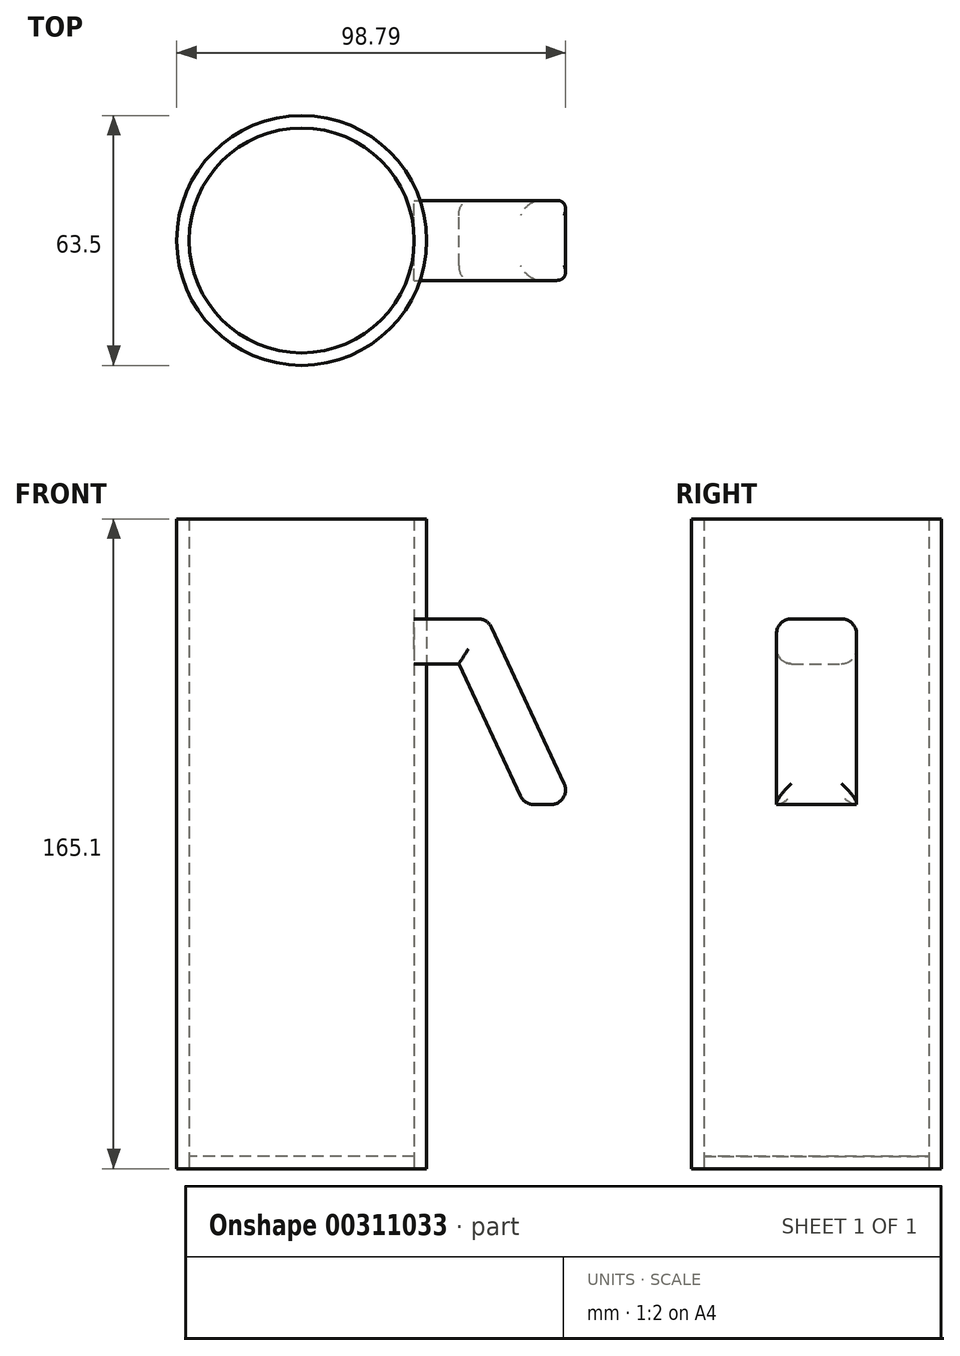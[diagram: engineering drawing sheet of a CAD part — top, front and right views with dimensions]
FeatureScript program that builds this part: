
annotation { "Feature Type Name" : "Feature", "Feature Type Description" : "" }
export const myFeature = defineFeature(function(context is Context, id is Id, definition is map)
    precondition{}
    {
        {
            var Q0;
            Q0=qCreatedBy(makeId("Top.planeOp"),FACE);
            var sketch = newSketch(context, id + "F0", { "sketchPlane" : qUnion([Q0])});
            skCircle(sketch, "E0", {"center": v(0, 0) * mm, "radius": 28.58 * mm});
            skCircle(sketch, "E1", {"center": v(0, 0) * mm, "radius": 31.75 * mm});
            skPoint(sketch, "E2.middle", {"position": v(31.75, 0) * mm});
            skSolve(sketch);
        }
        {
            var Q0;
            Q0=qCreatedBy(makeId("Front.planeOp"),FACE);
            var sketch = newSketch(context, id + "F1", { "sketchPlane" : qUnion([Q0])});
            skLineSegment(sketch, "E3.bottom", {"start": v(28.57, 128.27) * mm, "end": v(39.92, 128.27) * mm});
            skLineSegment(sketch, "E3.top", {"start": v(28.57, 139.7) * mm, "end": v(47.2, 139.7) * mm});
            skLineSegment(sketch, "E3.left", {"start": v(28.57, 128.27) * mm, "end": v(28.57, 139.7) * mm});
            skLineSegment(sketch, "E4", {"start": v(47.2, 139.7) * mm, "end": v(69.22, 92.49) * mm});
            skLineSegment(sketch, "E5", {"start": v(39.92, 128.27) * mm, "end": v(56.6, 92.49) * mm});
            skLineSegment(sketch, "E6", {"start": v(56.6, 92.49) * mm, "end": v(69.22, 92.49) * mm});
            skLineSegment(sketch, "E7", {"start": v(28.57, 0) * mm, "end": v(28.57, 165.1) * mm, "construction": true});
            skLineSegment(sketch, "E8", {"start": v(28.57, 165.1) * mm, "end": v(28.57, 139.7) * mm, "construction": true});
            skSolve(sketch);
        }
        {
            var Q0;
            Q0=makeQuery(id+"F0.imprint","IMPRINT",FACE,{"disambiguationData":[TD([[makeQuery(id+"F0.imprint","IMPRINT",EDGE,{"derivedFrom":sQuery(id+"F0.wireOp",EDGE,"E0")}),1.0]])]});
            extrude(context, id + "F2", {"entities" : qUnion([Q0]), "depth" : 3.17 * mm});
        }
        {
            var Q0;
            Q0=makeQuery(id+"F0.imprint","IMPRINT",FACE,{"disambiguationData":[TD([[makeQuery(id+"F0.imprint","IMPRINT",EDGE,{"derivedFrom":sQuery(id+"F0.wireOp",EDGE,"E0")}),-1.0]])]});
            extrude(context, id + "F3", {"entities" : qUnion([Q0]), "depth" : 165.1 * mm});
        }
        {
            var Q0;
            Q0=makeQuery(id+"F1.imprint","IMPRINT",FACE,{"disambiguationData":[TD([[makeQuery(id+"F1.imprint","IMPRINT",EDGE,{"derivedFrom":sQuery(id+"F1.wireOp",EDGE,"E3.bottom")}),1.0]])]});
            extrude(context, id + "F4", {"entities" : qUnion([Q0]), "endBound" : BoundingType.SYMMETRIC, "depth" : 20.32 * mm});
        }
        {
            var Q0;
            Q0=makeQuery(id+"F4.opExtrude","SWEPT_FACE",FACE,{"disambiguationData":[OSD([sQuery(id+"F1.wireOp",EDGE,"E4")])]});
            var Q1;
            Q1=makeQuery(id+"F4.opExtrude","SWEPT_EDGE",EDGE,{"disambiguationData":[OSD([sQuery(id+"F1.wireOp",EDGE,"E5"),sQuery(id+"F1.wireOp",EDGE,"E6")])]});
            var Q2;
            Q2=makeQuery(id+"F4.opExtrude","CAP_EDGE",EDGE,{"disambiguationData":[OSD([sQuery(id+"F1.wireOp",EDGE,"E5")])],"isStart":true});
            var Q3;
            Q3=makeQuery(id+"F4.opExtrude","CAP_EDGE",EDGE,{"disambiguationData":[OSD([sQuery(id+"F1.wireOp",EDGE,"E3.bottom")])],"isStart":true});
            var Q4;
            Q4=makeQuery(id+"F4.opExtrude","CAP_EDGE",EDGE,{"disambiguationData":[OSD([sQuery(id+"F1.wireOp",EDGE,"E3.top")])],"isStart":true});
            var Q5;
            Q5=makeQuery(id+"F4.opExtrude","CAP_EDGE",EDGE,{"disambiguationData":[OSD([sQuery(id+"F1.wireOp",EDGE,"E5")])],"isStart":false});
            var Q6;
            Q6=makeQuery(id+"F4.opExtrude","CAP_EDGE",EDGE,{"disambiguationData":[OSD([sQuery(id+"F1.wireOp",EDGE,"E3.bottom")])],"isStart":false});
            var Q7;
            Q7=makeQuery(id+"F4.opExtrude","CAP_EDGE",EDGE,{"disambiguationData":[OSD([sQuery(id+"F1.wireOp",EDGE,"E3.top")])],"isStart":false});
            fillet(context, id + "F5", {"entities" : qUnion([Q0, Q1, Q2, Q3, Q4, Q5, Q6, Q7]), "radius" : 3.8 * mm, "tangentPropagation" : true, "allowEdgeOverflow" : false});
        }
    });
